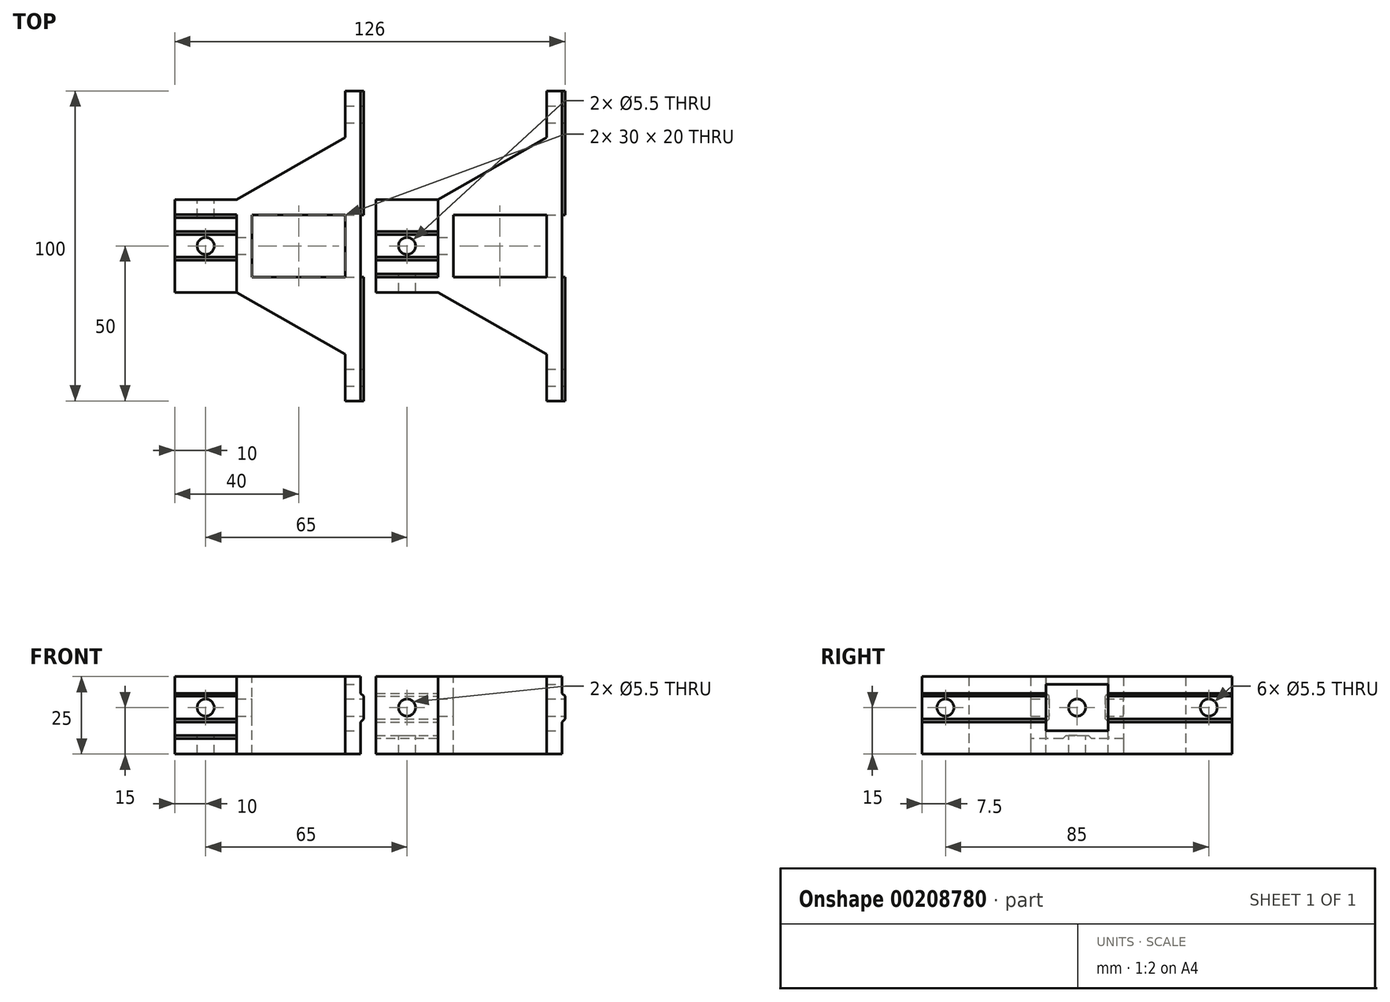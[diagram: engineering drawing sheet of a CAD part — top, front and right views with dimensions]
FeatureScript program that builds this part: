
annotation { "Feature Type Name" : "Feature", "Feature Type Description" : "" }
export const myFeature = defineFeature(function(context is Context, id is Id, definition is map)
    precondition{}
    {
        {
            var Q0;
            Q0=qCreatedBy(makeId("Top.planeOp"),FACE);
            var sketch = newSketch(context, id + "F0", { "sketchPlane" : qUnion([Q0])});
            skLineSegment(sketch, "E0.bottom", {"start": v(20, -50) * mm, "end": v(15, -50) * mm});
            skLineSegment(sketch, "E0.top", {"start": v(20, 50) * mm, "end": v(15, 50) * mm});
            skLineSegment(sketch, "E0.left", {"start": v(20, -50) * mm, "end": v(20, 50) * mm});
            skLineSegment(sketch, "E0.right", {"start": v(-20, -50) * mm, "end": v(-20, -15) * mm, "construction": true});
            skPoint(sketch, "E0.middle", {"position": v(0, 0) * mm});
            skLineSegment(sketch, "E1", {"start": v(15, 50) * mm, "end": v(-20, 50) * mm, "construction": true});
            skLineSegment(sketch, "E2", {"start": v(-20, 15) * mm, "end": v(-20, 50) * mm, "construction": true});
            skLineSegment(sketch, "E3", {"start": v(-20, -15) * mm, "end": v(-20, -10) * mm});
            skLineSegment(sketch, "E4", {"start": v(15, -50) * mm, "end": v(-20, -50) * mm, "construction": true});
            skLineSegment(sketch, "E5", {"start": v(15, 50) * mm, "end": v(15, 35) * mm});
            skLineSegment(sketch, "E6", {"start": v(-20, -15) * mm, "end": v(15, -35) * mm});
            skLineSegment(sketch, "E7", {"start": v(15, -35) * mm, "end": v(15, -50) * mm});
            skLineSegment(sketch, "E8", {"start": v(15, 35) * mm, "end": v(-20, 15) * mm});
            skLineSegment(sketch, "E9", {"start": v(-20, 10) * mm, "end": v(-20, 15) * mm});
            skLineSegment(sketch, "E10", {"start": v(-20, -10) * mm, "end": v(-20, 10) * mm});
            skSolve(sketch);
        }
        {
            var Q0;
            Q0=makeQuery(id+"F0.imprint","IMPRINT",FACE,{"disambiguationData":[TD([[makeQuery(id+"F0.imprint","IMPRINT",EDGE,{"derivedFrom":sQuery(id+"F0.wireOp",EDGE,"E0.bottom")}),-1.0]])]});
            extrude(context, id + "F1", {"entities" : qUnion([Q0]), "depth" : 25 * mm});
        }
        {
            var Q0;
            Q0=makeQuery(id+"F1.opExtrude","SWEPT_FACE",FACE,{"disambiguationData":[OSD([sQuery(id+"F0.wireOp",EDGE,"E0.bottom")])]});
            var sketch = newSketch(context, id + "F2", { "sketchPlane" : qUnion([Q0])});
            skLineSegment(sketch, "E11", {"start": v(20, 19.64) * mm, "end": v(21, 18.64) * mm});
            skLineSegment(sketch, "E12", {"start": v(21, 18.64) * mm, "end": v(21.8, 17.84) * mm, "construction": true});
            skLineSegment(sketch, "E13", {"start": v(21.8, 17.84) * mm, "end": v(24.64, 15) * mm, "construction": true});
            skLineSegment(sketch, "E14", {"start": v(24.64, 15) * mm, "end": v(21.8, 12.16) * mm, "construction": true});
            skLineSegment(sketch, "E15", {"start": v(21.8, 12.16) * mm, "end": v(21, 11.36) * mm, "construction": true});
            skLineSegment(sketch, "E16", {"start": v(21, 11.36) * mm, "end": v(20, 10.36) * mm});
            skLineSegment(sketch, "E17", {"start": v(21, 11.36) * mm, "end": v(21, 18.64) * mm});
            skLineSegment(sketch, "E18", {"start": v(21.8, 17.84) * mm, "end": v(21.8, 12.16) * mm, "construction": true});
            skLineSegment(sketch, "E19", {"start": v(20, 0) * mm, "end": v(20, 5) * mm});
            skLineSegment(sketch, "E20", {"start": v(20, 5) * mm, "end": v(20, 25) * mm});
            skLineSegment(sketch, "E21", {"start": v(21, 15) * mm, "end": v(20, 15) * mm, "construction": true});
            skSolve(sketch);
        }
        {
            var Q0;
            {var subQ0=sQuery(id+"F2.wireOp",EDGE,"E11");Q0=makeQuery(id+"F2.imprint","IMPRINT",FACE,{"disambiguationData":[TD([[makeQuery(id+"F2.imprint","IMPRINT",EDGE,{"derivedFrom":subQ0}),-1.0]])]});}
            var Q1;
            Q1=makeQuery(id+"F1.opExtrude","SWEPT_FACE",FACE,{"disambiguationData":[OSD([sQuery(id+"F0.wireOp",EDGE,"E0.top")])]});
            extrude(context, id + "F3", {"entities" : qUnion([Q0]), "operationType" : NewBodyOperationType.ADD, "endBound" : BoundingType.UP_TO_SURFACE, "oppositeDirection" : true, "endBoundEntityFace" : qUnion([Q1]), "depth" : 25 * mm});
        }
        {
            var Q0;
            Q0=makeQuery(id+"F3.opExtrude","SWEPT_FACE",FACE,{"disambiguationData":[OSD([sQuery(id+"F2.wireOp",EDGE,"E17")])]});
            var sketch = newSketch(context, id + "F4", { "sketchPlane" : qUnion([Q0])});
            skLineSegment(sketch, "E22.bottom", {"start": v(-10, 22.5) * mm, "end": v(10, 22.5) * mm});
            skLineSegment(sketch, "E22.top", {"start": v(-10, 7.5) * mm, "end": v(10, 7.5) * mm});
            skLineSegment(sketch, "E22.left", {"start": v(-10, 22.5) * mm, "end": v(-10, 7.5) * mm});
            skLineSegment(sketch, "E22.right", {"start": v(10, 22.5) * mm, "end": v(10, 7.5) * mm});
            skLineSegment(sketch, "E23", {"start": v(0, 22.5) * mm, "end": v(0, 25) * mm, "construction": true});
            skLineSegment(sketch, "E24.bottom", {"start": v(-50.13, 0) * mm, "end": v(50, 0) * mm, "construction": true});
            skLineSegment(sketch, "E24.top", {"start": v(-50.13, 5) * mm, "end": v(50, 5) * mm, "construction": true});
            skLineSegment(sketch, "E24.left", {"start": v(-50.13, 0) * mm, "end": v(-50.13, 5) * mm, "construction": true});
            skLineSegment(sketch, "E24.right", {"start": v(50, 0) * mm, "end": v(50, 5) * mm, "construction": true});
            skLineSegment(sketch, "E25", {"start": v(0, 7.5) * mm, "end": v(0, 5) * mm, "construction": true});
            skSolve(sketch);
        }
        {
            var Q0;
            Q0=makeQuery(id+"F4.imprint","IMPRINT",FACE,{"disambiguationData":[TD([[makeQuery(id+"F4.imprint","IMPRINT",EDGE,{"derivedFrom":sQuery(id+"F4.wireOp",EDGE,"E22.bottom")}),-1.0]])]});
            var Q1;
            {var subQ0=sQuery(id+"F4.wireOp",EDGE,"E22.top");Q1=makeQuery(id+"F4.imprint","IMPRINT",FACE,{"disambiguationData":[TD([[makeQuery(id+"F4.imprint","IMPRINT",EDGE,{"derivedFrom":subQ0}),1.0]])]});}
            var Q2;
            {var subQ0=sQuery(id+"F4.wireOp",EDGE,"E22.left");var subQ1=sQuery(id+"F2.wireOp",EDGE,"E17");var subQ2=makeQuery(id+"F3.opExtrude","SWEPT_EDGE",EDGE,{"disambiguationData":[OSD([sQuery(id+"F2.wireOp",EDGE,"E11"),subQ1])]});var subQ3=makeQuery(id+"F4.imprint","INTERSECT",VERTEX,{"derivedFrom":[subQ2,subQ0]});Q2=makeQuery(id+"F4.imprint","IMPRINT",FACE,{"disambiguationData":[TD([[makeQuery(id+"F4.imprint","IMPRINT",EDGE,{"disambiguationData":[TD([[subQ3,-1.0]])],"derivedFrom":subQ0}),1.0]])]});}
            var Q3;
            Q3=sQuery(id+"F4.wireOp",EDGE,"E23");
            var Q4;
            Q4=sQuery(id+"F4.wireOp",EDGE,"nOt40Ara-Swmj-gLWi-o4nC-cXzWa2sV8QlZ");
            extrude(context, id + "F5", {"entities" : qUnion([Q0, Q1, Q2]), "operationType" : NewBodyOperationType.REMOVE, "surfaceEntities" : qUnion([Q3, Q4]), "oppositeDirection" : true, "depth" : 35 * mm, "hasSecondDirection" : true, "secondDirectionOppositeDirection" : false, "secondDirectionDepth" : 10 * mm});
        }
        {
            var Q0;
            Q0=makeQuery(id+"F1.opExtrude","CAP_FACE",FACE,{"disambiguationData":[OSD([sQuery(id+"F0.wireOp",EDGE,"E0.bottom"),sQuery(id+"F0.wireOp",EDGE,"E0.top"),sQuery(id+"F0.wireOp",EDGE,"E0.left"),sQuery(id+"F0.wireOp",EDGE,"E3"),sQuery(id+"F0.wireOp",EDGE,"E5"),sQuery(id+"F0.wireOp",EDGE,"E6")])],"isStart":false});
            var sketch = newSketch(context, id + "F6", { "sketchPlane" : qUnion([Q0])});
            skLineSegment(sketch, "E26.bottom", {"start": v(15, -10) * mm, "end": v(-15, -10) * mm});
            skLineSegment(sketch, "E26.top", {"start": v(15, 10) * mm, "end": v(-15, 10) * mm});
            skLineSegment(sketch, "E26.left", {"start": v(15, -10) * mm, "end": v(15, 10) * mm});
            skLineSegment(sketch, "E26.right", {"start": v(-15, -10) * mm, "end": v(-15, 10) * mm});
            skPoint(sketch, "E26.middle", {"position": v(0, 0) * mm});
            skLineSegment(sketch, "E27", {"start": v(15, 0) * mm, "end": v(20, 0) * mm, "construction": true});
            skLineSegment(sketch, "E28", {"start": v(-15, 0) * mm, "end": v(-20, 0) * mm, "construction": true});
            skSolve(sketch);
        }
        {
            var Q0;
            Q0=makeQuery(id+"F6.imprint","IMPRINT",FACE,{"disambiguationData":[TD([[makeQuery(id+"F6.imprint","IMPRINT",EDGE,{"derivedFrom":sQuery(id+"F6.wireOp",EDGE,"E26.bottom")}),-1.0]])]});
            extrude(context, id + "F7", {"entities" : qUnion([Q0]), "operationType" : NewBodyOperationType.REMOVE, "endBound" : BoundingType.THROUGH_ALL, "oppositeDirection" : true, "depth" : 25 * mm});
        }
        {
            var Q0;
            Q0=makeQuery(id+"F1.opExtrude","SWEPT_FACE",FACE,{"disambiguationData":[OSD([sQuery(id+"F0.wireOp",EDGE,"E5")])]});
            var sketch = newSketch(context, id + "F8", { "sketchPlane" : qUnion([Q0])});
            skPoint(sketch, "E29", {"position": v(-42.5, 15) * mm});
            skPoint(sketch, "E30", {"position": v(42.5, 15) * mm});
            skLineSegment(sketch, "E31", {"start": v(-42.5, 25) * mm, "end": v(-42.5, 5) * mm});
            skLineSegment(sketch, "E32", {"start": v(-42.5, 5) * mm, "end": v(-42.5, 0) * mm});
            skLineSegment(sketch, "E33", {"start": v(42.5, 25) * mm, "end": v(42.5, 5) * mm, "construction": true});
            skLineSegment(sketch, "E34", {"start": v(42.5, 5) * mm, "end": v(42.5, 0) * mm, "construction": true});
            skSolve(sketch);
        }
        {
            var Q0;
            Q0=makeQuery(id+"F1.opExtrude","SWEPT_FACE",FACE,{"disambiguationData":[OSD([sQuery(id+"F0.wireOp",EDGE,"E3")])]});
            var sketch = newSketch(context, id + "F9", { "sketchPlane" : qUnion([Q0])});
            skPoint(sketch, "E35", {"position": v(0, 15) * mm});
            skLineSegment(sketch, "E36.bottom", {"start": v(-15, 25) * mm, "end": v(15, 25) * mm, "construction": true});
            skLineSegment(sketch, "E36.top", {"start": v(-15, 5) * mm, "end": v(15, 5) * mm, "construction": true});
            skLineSegment(sketch, "E36.left", {"start": v(-15, 25) * mm, "end": v(-15, 5) * mm, "construction": true});
            skLineSegment(sketch, "E36.right", {"start": v(15, 25) * mm, "end": v(15, 5) * mm, "construction": true});
            skLineSegment(sketch, "E37", {"start": v(0, 5) * mm, "end": v(0, 0) * mm, "construction": true});
            skLineSegment(sketch, "E38", {"start": v(15, 15) * mm, "end": v(-15, 15) * mm, "construction": true});
            skSolve(sketch);
        }
        {
            var Q0;
            Q0=sQuery(id+"F8.wireOp",VERTEX,"E29");
            var Q1;
            Q1=sQuery(id+"F9.wireOp",VERTEX,"E35");
            var Q2;
            Q2=sQuery(id+"F8.wireOp",VERTEX,"E30");
            var Q3;
            Q3=makeQuery(id+"F1.opExtrude","SWEPT_BODY",BODY,{"disambiguationData":[OSD([sQuery(id+"F0.wireOp",EDGE,"E0.bottom"),sQuery(id+"F0.wireOp",EDGE,"E0.top"),sQuery(id+"F0.wireOp",EDGE,"E0.left"),sQuery(id+"F0.wireOp",EDGE,"E3"),sQuery(id+"F0.wireOp",EDGE,"E5"),sQuery(id+"F0.wireOp",EDGE,"E6"),sQuery(id+"F0.wireOp",EDGE,"E7"),sQuery(id+"F0.wireOp",EDGE,"E8")])]});
            hole(context, id + "F10", {"style" : HoleStyle.SIMPLE, "endStyle" : HoleEndStyle.THROUGH, "standardTappedOrClearance" : lookupTablePath({ "standard" : "ISO", "fit" : "Normal", "size" : "M5", "type" : "Clearance" }), "standardBlindInLast" : lookupTablePath({ "fit" : "Standard", "standard" : "ISO", "size" : "M5", "type" : "Clearance" }), "holeDiameter" : 5.5 * mm, "locations" : qUnion([Q0, Q1, Q2]), "scope" : qUnion([Q3]), "isTappedThrough" : true});
        }
        {
            var Q0;
            Q0=makeQuery(id+"F1.opExtrude","SWEPT_FACE",FACE,{"disambiguationData":[OSD([sQuery(id+"F0.wireOp",EDGE,"E3"),sQuery(id+"F0.wireOp",EDGE,"E9"),sQuery(id+"F0.wireOp",EDGE,"E10")])]});
            var sketch = newSketch(context, id + "F11", { "sketchPlane" : qUnion([Q0])});
            skLineSegment(sketch, "E39.top", {"start": v(-10.1, 5) * mm, "end": v(10.1, 5) * mm});
            skLineSegment(sketch, "E39.left", {"start": v(-10.1, 25) * mm, "end": v(-10.1, 5) * mm});
            skLineSegment(sketch, "E39.right", {"start": v(10.1, 25) * mm, "end": v(10.1, 5) * mm});
            skLineSegment(sketch, "E40.bottom", {"start": v(15, 0) * mm, "end": v(-15, 0) * mm});
            skLineSegment(sketch, "E40.left", {"start": v(15, 0) * mm, "end": v(15, 25) * mm});
            skLineSegment(sketch, "E40.right", {"start": v(-15, 0) * mm, "end": v(-15, 25) * mm});
            skLineSegment(sketch, "E41", {"start": v(-10.1, 25) * mm, "end": v(-15, 25) * mm});
            skLineSegment(sketch, "E42", {"start": v(10.1, 25) * mm, "end": v(15, 25) * mm});
            skLineSegment(sketch, "E43", {"start": v(-4.64, 5) * mm, "end": v(-3.64, 6) * mm});
            skLineSegment(sketch, "E44", {"start": v(-3.64, 6) * mm, "end": v(-2.84, 6.8) * mm, "construction": true});
            skLineSegment(sketch, "E45", {"start": v(-2.84, 6.8) * mm, "end": v(0, 9.64) * mm, "construction": true});
            skLineSegment(sketch, "E46", {"start": v(0, 9.64) * mm, "end": v(2.84, 6.8) * mm, "construction": true});
            skLineSegment(sketch, "E47", {"start": v(2.84, 6.8) * mm, "end": v(3.64, 6) * mm, "construction": true});
            skLineSegment(sketch, "E48", {"start": v(3.64, 6) * mm, "end": v(4.64, 5) * mm});
            skLineSegment(sketch, "E49", {"start": v(3.64, 6) * mm, "end": v(-3.64, 6) * mm});
            skLineSegment(sketch, "E50", {"start": v(-2.84, 6.8) * mm, "end": v(2.84, 6.8) * mm, "construction": true});
            skLineSegment(sketch, "E51", {"start": v(0, 6) * mm, "end": v(0, 5) * mm, "construction": true});
            skLineSegment(sketch, "E52", {"start": v(-10.1, 19.64) * mm, "end": v(-9.1, 18.64) * mm});
            skLineSegment(sketch, "E53", {"start": v(-9.1, 18.64) * mm, "end": v(-8.3, 17.84) * mm, "construction": true});
            skLineSegment(sketch, "E54", {"start": v(-8.3, 17.84) * mm, "end": v(-5.46, 15) * mm, "construction": true});
            skLineSegment(sketch, "E55", {"start": v(-5.46, 15) * mm, "end": v(-8.3, 12.16) * mm, "construction": true});
            skLineSegment(sketch, "E56", {"start": v(-8.3, 12.16) * mm, "end": v(-9.1, 11.36) * mm, "construction": true});
            skLineSegment(sketch, "E57", {"start": v(-9.1, 11.36) * mm, "end": v(-10.1, 10.36) * mm});
            skLineSegment(sketch, "E58", {"start": v(-9.1, 11.36) * mm, "end": v(-9.1, 18.64) * mm});
            skLineSegment(sketch, "E59", {"start": v(-8.3, 12.16) * mm, "end": v(-8.3, 17.84) * mm, "construction": true});
            skLineSegment(sketch, "E60", {"start": v(-9.1, 15) * mm, "end": v(-10.1, 15) * mm, "construction": true});
            skLineSegment(sketch, "E61", {"start": v(10.1, 10.36) * mm, "end": v(9.1, 11.36) * mm});
            skLineSegment(sketch, "E62", {"start": v(9.1, 11.36) * mm, "end": v(8.3, 12.16) * mm, "construction": true});
            skLineSegment(sketch, "E63", {"start": v(8.3, 12.16) * mm, "end": v(5.46, 15) * mm, "construction": true});
            skLineSegment(sketch, "E64", {"start": v(5.46, 15) * mm, "end": v(8.3, 17.84) * mm, "construction": true});
            skLineSegment(sketch, "E65", {"start": v(8.3, 17.84) * mm, "end": v(9.1, 18.64) * mm, "construction": true});
            skLineSegment(sketch, "E66", {"start": v(9.1, 18.64) * mm, "end": v(10.1, 19.64) * mm});
            skLineSegment(sketch, "E67", {"start": v(9.1, 11.36) * mm, "end": v(9.1, 18.64) * mm});
            skLineSegment(sketch, "E68", {"start": v(8.3, 12.16) * mm, "end": v(8.3, 17.84) * mm, "construction": true});
            skLineSegment(sketch, "E69", {"start": v(9.1, 15) * mm, "end": v(10.1, 15) * mm, "construction": true});
            skSolve(sketch);
        }
        {
            var Q0;
            Q0=makeQuery(id+"F11.imprint","IMPRINT",FACE,{"disambiguationData":[TD([[makeQuery(id+"F11.imprint","IMPRINT",EDGE,{"derivedFrom":sQuery(id+"F11.wireOp",EDGE,"E40.bottom")}),-1.0]])]});
            var Q1;
            {var subQ0=sQuery(id+"F11.wireOp",EDGE,"E52");Q1=makeQuery(id+"F11.imprint","IMPRINT",FACE,{"disambiguationData":[TD([[makeQuery(id+"F11.imprint","IMPRINT",EDGE,{"derivedFrom":subQ0}),-1.0]])]});}
            var Q2;
            {var subQ0=sQuery(id+"F11.wireOp",EDGE,"E43");Q2=makeQuery(id+"F11.imprint","IMPRINT",FACE,{"disambiguationData":[TD([[makeQuery(id+"F11.imprint","IMPRINT",EDGE,{"derivedFrom":subQ0}),-1.0]])]});}
            var Q3;
            {var subQ0=sQuery(id+"F11.wireOp",EDGE,"E61");Q3=makeQuery(id+"F11.imprint","IMPRINT",FACE,{"disambiguationData":[TD([[makeQuery(id+"F11.imprint","IMPRINT",EDGE,{"derivedFrom":subQ0}),-1.0]])]});}
            var Q4;
            Q4=sQuery(id+"F11.wireOp",EDGE,"E69");
            var Q5;
            Q5=sQuery(id+"F11.wireOp",EDGE,"E68");
            var Q6;
            Q6=sQuery(id+"F11.wireOp",EDGE,"E63");
            var Q7;
            Q7=sQuery(id+"F11.wireOp",EDGE,"E64");
            var Q8;
            Q8=sQuery(id+"F11.wireOp",EDGE,"E65");
            var Q9;
            Q9=sQuery(id+"F11.wireOp",EDGE,"E62");
            extrude(context, id + "F12", {"entities" : qUnion([Q0, Q1, Q2, Q3]), "operationType" : NewBodyOperationType.ADD, "surfaceEntities" : qUnion([Q4, Q5, Q6, Q7, Q8, Q9]), "depth" : 20 * mm});
        }
        {
            var Q0;
            Q0=makeQuery(id+"F12.boolean.opBoolean","MERGE",FACE,{"derivedFrom":[makeQuery(id+"F1.opExtrude","CAP_FACE",FACE,{"disambiguationData":[OSD([sQuery(id+"F0.wireOp",EDGE,"E0.bottom"),sQuery(id+"F0.wireOp",EDGE,"E0.top"),sQuery(id+"F0.wireOp",EDGE,"E0.left"),sQuery(id+"F0.wireOp",EDGE,"E3"),sQuery(id+"F0.wireOp",EDGE,"E5"),sQuery(id+"F0.wireOp",EDGE,"E6"),sQuery(id+"F0.wireOp",EDGE,"E7"),sQuery(id+"F0.wireOp",EDGE,"E8"),sQuery(id+"F0.wireOp",EDGE,"E9"),sQuery(id+"F0.wireOp",EDGE,"E10")])],"isStart":true}),makeQuery(id+"F12.opExtrude","SWEPT_FACE",FACE,{"disambiguationData":[OSD([sQuery(id+"F11.wireOp",EDGE,"E40.bottom")])]})]});
            var sketch = newSketch(context, id + "F13", { "sketchPlane" : qUnion([Q0])});
            skLineSegment(sketch, "E70", {"start": v(-30, -15) * mm, "end": v(-30, 15) * mm, "construction": true});
            skPoint(sketch, "E71", {"position": v(-30, 0) * mm});
            skSolve(sketch);
        }
        {
            var Q0;
            Q0=makeQuery(id+"F12.opExtrude","SWEPT_FACE",FACE,{"disambiguationData":[OSD([sQuery(id+"F11.wireOp",EDGE,"E40.left")])]});
            var sketch = newSketch(context, id + "F14", { "sketchPlane" : qUnion([Q0])});
            skLineSegment(sketch, "E72", {"start": v(-30, 5) * mm, "end": v(-30, 25) * mm, "construction": true});
            skPoint(sketch, "E73", {"position": v(-30, 15) * mm});
            skLineSegment(sketch, "E74", {"start": v(-30, 5) * mm, "end": v(-30, 0) * mm, "construction": true});
            skSolve(sketch);
        }
        {
            var Q0;
            Q0=sQuery(id+"F14.wireOp",VERTEX,"E73");
            var Q1;
            Q1=sQuery(id+"F13.wireOp",VERTEX,"E71");
            var Q2;
            Q2=makeQuery(id+"F1.opExtrude","SWEPT_BODY",BODY,{"disambiguationData":[OSD([sQuery(id+"F0.wireOp",EDGE,"E0.bottom"),sQuery(id+"F0.wireOp",EDGE,"E0.top"),sQuery(id+"F0.wireOp",EDGE,"E0.left"),sQuery(id+"F0.wireOp",EDGE,"E3"),sQuery(id+"F0.wireOp",EDGE,"E5"),sQuery(id+"F0.wireOp",EDGE,"E6"),sQuery(id+"F0.wireOp",EDGE,"E7"),sQuery(id+"F0.wireOp",EDGE,"E8"),sQuery(id+"F0.wireOp",EDGE,"E9"),sQuery(id+"F0.wireOp",EDGE,"E10")])]});
            hole(context, id + "F15", {"style" : HoleStyle.SIMPLE, "endStyle" : HoleEndStyle.THROUGH, "standardTappedOrClearance" : lookupTablePath({ "standard" : "ISO", "fit" : "Normal", "size" : "M5", "type" : "Clearance" }), "standardBlindInLast" : lookupTablePath({ "fit" : "Standard", "standard" : "ISO", "size" : "M5", "type" : "Clearance" }), "holeDiameter" : 5.5 * mm, "locations" : qUnion([Q0, Q1]), "scope" : qUnion([Q2]), "isTappedThrough" : true});
        }
        {
            var Q0;
            Q0=makeQuery(id+"F1.opExtrude","SWEPT_BODY",BODY,{"disambiguationData":[OSD([sQuery(id+"F0.wireOp",EDGE,"E0.bottom"),sQuery(id+"F0.wireOp",EDGE,"E0.top"),sQuery(id+"F0.wireOp",EDGE,"E0.left"),sQuery(id+"F0.wireOp",EDGE,"E3"),sQuery(id+"F0.wireOp",EDGE,"E5"),sQuery(id+"F0.wireOp",EDGE,"E6"),sQuery(id+"F0.wireOp",EDGE,"E7"),sQuery(id+"F0.wireOp",EDGE,"E8"),sQuery(id+"F0.wireOp",EDGE,"E9"),sQuery(id+"F0.wireOp",EDGE,"E10")])]});
            transform(context, id + "F16", {"entities" : qUnion([Q0]), "transformType" : TransformType.TRANSLATION_3D, "dx" : 65 * mm, "dy" : 0 * mm, "dz" : 0 * mm, "makeCopy" : true});
        }
        {
            var Q0;
            Q0=makeQuery(id+"F12.opExtrude","SWEPT_FACE",FACE,{"disambiguationData":[OSD([sQuery(id+"F11.wireOp",EDGE,"E40.left")])]});
            var sketch = newSketch(context, id + "F17", { "sketchPlane" : qUnion([Q0])});
            skLineSegment(sketch, "E75.bottom", {"start": v(-40, 25) * mm, "end": v(-20, 25) * mm});
            skLineSegment(sketch, "E75.top", {"start": v(-40, 5) * mm, "end": v(-20, 5) * mm});
            skLineSegment(sketch, "E75.left", {"start": v(-40, 25) * mm, "end": v(-40, 5) * mm});
            skLineSegment(sketch, "E75.right", {"start": v(-20, 25) * mm, "end": v(-20, 5) * mm});
            skSolve(sketch);
        }
        {
            var Q0;
            Q0=makeQuery(id+"F17.imprint","IMPRINT",FACE,{"disambiguationData":[TD([[makeQuery(id+"F17.imprint","IMPRINT",EDGE,{"derivedFrom":sQuery(id+"F17.wireOp",EDGE,"E75.bottom")}),-1.0]])]});
            var Q1;
            Q1=makeQuery(id+"F12.opExtrude","SWEPT_FACE",FACE,{"disambiguationData":[OSD([sQuery(id+"F11.wireOp",EDGE,"E67")])]});
            extrude(context, id + "F18", {"entities" : qUnion([Q0]), "operationType" : NewBodyOperationType.REMOVE, "endBound" : BoundingType.UP_TO_SURFACE, "oppositeDirection" : true, "endBoundEntityFace" : qUnion([Q1]), "depth" : 25 * mm});
        }
        {
            var Q0;
            Q0=makeQuery(id+"F16.opPattern","COPY",FACE,{"derivedFrom":makeQuery(id+"F12.opExtrude","SWEPT_FACE",FACE,{"disambiguationData":[OSD([sQuery(id+"F11.wireOp",EDGE,"E40.right")])]}),"instanceName":"1"});
            var sketch = newSketch(context, id + "F19", { "sketchPlane" : qUnion([Q0])});
            skLineSegment(sketch, "E76.bottom", {"start": v(-45, 25) * mm, "end": v(-25, 25) * mm});
            skLineSegment(sketch, "E76.top", {"start": v(-45, 5) * mm, "end": v(-25, 5) * mm});
            skLineSegment(sketch, "E76.left", {"start": v(-45, 25) * mm, "end": v(-45, 5) * mm});
            skLineSegment(sketch, "E76.right", {"start": v(-25, 25) * mm, "end": v(-25, 5) * mm});
            skSolve(sketch);
        }
        {
            var Q0;
            Q0=makeQuery(id+"F19.imprint","IMPRINT",FACE,{"disambiguationData":[TD([[makeQuery(id+"F19.imprint","IMPRINT",EDGE,{"derivedFrom":sQuery(id+"F19.wireOp",EDGE,"E76.bottom")}),1.0]])]});
            var Q1;
            Q1=makeQuery(id+"F16.opPattern","COPY",FACE,{"derivedFrom":makeQuery(id+"F12.opExtrude","SWEPT_FACE",FACE,{"disambiguationData":[OSD([sQuery(id+"F11.wireOp",EDGE,"E58")])]}),"instanceName":"1"});
            extrude(context, id + "F20", {"entities" : qUnion([Q0]), "operationType" : NewBodyOperationType.REMOVE, "endBound" : BoundingType.UP_TO_SURFACE, "oppositeDirection" : true, "endBoundEntityFace" : qUnion([Q1]), "depth" : 25 * mm});
        }
    });
